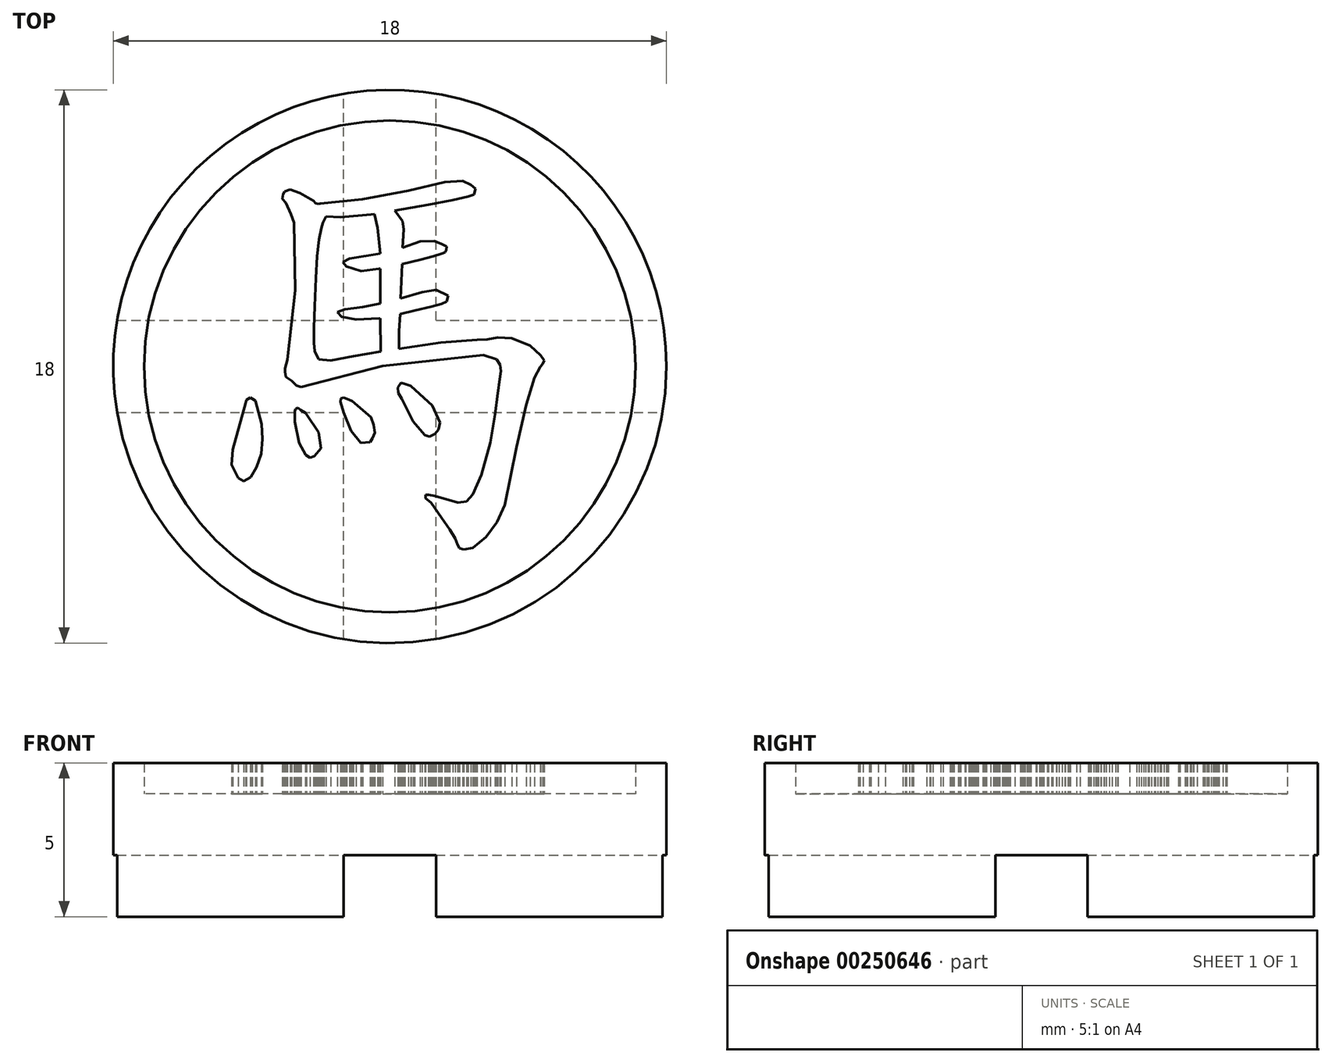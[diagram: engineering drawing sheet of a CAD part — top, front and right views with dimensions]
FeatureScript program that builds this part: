
annotation { "Feature Type Name" : "Feature", "Feature Type Description" : "" }
export const myFeature = defineFeature(function(context is Context, id is Id, definition is map)
    precondition{}
    {
        {
            var Q0;
            Q0=qCreatedBy(makeId("Top.planeOp"),FACE);
            var sketch = newSketch(context, id + "F0", { "sketchPlane" : qUnion([Q0])});
            skCircle(sketch, "E0", {"center": v(-31.33, 19.76) * mm, "radius": 9 * mm});
            skSolve(sketch);
        }
        {
            var Q0;
            Q0=qSketchRegion(id+"F0",true);
            extrude(context, id + "F1", {"entities" : qUnion([Q0]), "depth" : 4 * mm});
        }
        {
            var Q0;
            Q0=makeQuery(id+"F1.opExtrude","CAP_FACE",FACE,{"disambiguationData":[OSD([sQuery(id+"F0.wireOp",EDGE,"E0")])],"isStart":false});
            var sketch = newSketch(context, id + "F2", { "sketchPlane" : qUnion([Q0])});
            skCircle(sketch, "E1", {"center": v(-31.33, 19.76) * mm, "radius": 8 * mm});
            skCircle(sketch, "E2", {"center": v(-31.33, 19.76) * mm, "radius": 9 * mm});
            skSolve(sketch);
        }
        {
            var Q0;
            Q0=makeQuery(id+"F1.opExtrude","CAP_FACE",FACE,{"disambiguationData":[OSD([sQuery(id+"F0.wireOp",EDGE,"E0")])],"isStart":true});
            var sketch = newSketch(context, id + "F3", { "sketchPlane" : qUnion([Q0])});
            skLineSegment(sketch, "E3", {"start": v(-31.33, -19.76) * mm, "end": v(-22.33, -19.76) * mm, "construction": true});
            skLineSegment(sketch, "E4", {"start": v(-31.33, -19.76) * mm, "end": v(-31.33, -10.76) * mm, "construction": true});
            skLineSegment(sketch, "E5", {"start": v(-31.33, -19.76) * mm, "end": v(-40.33, -19.76) * mm, "construction": true});
            skLineSegment(sketch, "E6", {"start": v(-31.33, -19.76) * mm, "end": v(-31.33, -28.76) * mm, "construction": true});
            skLineSegment(sketch, "E7.bottom", {"start": v(-40.33, -28.76) * mm, "end": v(-22.33, -28.76) * mm});
            skLineSegment(sketch, "E7.top", {"start": v(-40.33, -10.76) * mm, "end": v(-22.33, -10.76) * mm});
            skLineSegment(sketch, "E7.left", {"start": v(-22.33, -10.76) * mm, "end": v(-22.33, -28.76) * mm});
            skLineSegment(sketch, "E7.right", {"start": v(-40.33, -10.76) * mm, "end": v(-40.33, -28.76) * mm});
            skPoint(sketch, "E8", {"position": v(-31.33, -28.76) * mm});
            skPoint(sketch, "E9", {"position": v(-40.33, -19.76) * mm});
            skPoint(sketch, "E10", {"position": v(-22.33, -19.76) * mm});
            skPoint(sketch, "E11", {"position": v(-31.33, -10.76) * mm});
            skLineSegment(sketch, "E12.bottom", {"start": v(-32.83, -10.76) * mm, "end": v(-29.83, -10.76) * mm});
            skLineSegment(sketch, "E12.top", {"start": v(-32.83, -28.76) * mm, "end": v(-29.83, -28.76) * mm});
            skLineSegment(sketch, "E12.left", {"start": v(-32.83, -10.76) * mm, "end": v(-32.83, -28.76) * mm});
            skLineSegment(sketch, "E12.right", {"start": v(-29.83, -10.76) * mm, "end": v(-29.83, -28.76) * mm});
            skLineSegment(sketch, "E13.bottom", {"start": v(-40.33, -18.26) * mm, "end": v(-22.33, -18.26) * mm});
            skLineSegment(sketch, "E13.top", {"start": v(-40.33, -21.26) * mm, "end": v(-22.33, -21.26) * mm});
            skLineSegment(sketch, "E13.left", {"start": v(-40.33, -18.26) * mm, "end": v(-40.33, -21.26) * mm});
            skLineSegment(sketch, "E13.right", {"start": v(-22.33, -18.26) * mm, "end": v(-22.33, -21.26) * mm});
            skSolve(sketch);
        }
        {
            var Q0;
            {var subQ1=sQuery(id+"F3.wireOp",EDGE,"E12.bottom");var subQ3=makeQuery(id+"F1.opExtrude","CAP_EDGE",EDGE,{"disambiguationData":[OSD([sQuery(id+"F0.wireOp",EDGE,"E0")])],"isStart":true});var subQ4=makeQuery(id+"F3.imprint","INTERSECT",VERTEX,{"derivedFrom":[subQ3,subQ1]});Q0=makeQuery(id+"F3.imprint","IMPRINT",FACE,{"disambiguationData":[TD([[makeQuery(id+"F3.imprint","IMPRINT",EDGE,{"disambiguationData":[TD([[subQ4,1.0]])],"derivedFrom":subQ3}),1.0]])]});}
            var Q1;
            {var subQ1=sQuery(id+"F3.wireOp",EDGE,"E12.bottom");var subQ3=makeQuery(id+"F1.opExtrude","CAP_EDGE",EDGE,{"disambiguationData":[OSD([sQuery(id+"F0.wireOp",EDGE,"E0")])],"isStart":true});var subQ4=makeQuery(id+"F3.imprint","INTERSECT",VERTEX,{"derivedFrom":[subQ3,subQ1]});Q1=makeQuery(id+"F3.imprint","IMPRINT",FACE,{"disambiguationData":[TD([[makeQuery(id+"F3.imprint","IMPRINT",EDGE,{"disambiguationData":[TD([[subQ4,-1.0]])],"derivedFrom":subQ3}),1.0]])]});}
            var Q2;
            {var subQ1=sQuery(id+"F3.wireOp",EDGE,"E12.top");var subQ3=makeQuery(id+"F1.opExtrude","CAP_EDGE",EDGE,{"disambiguationData":[OSD([sQuery(id+"F0.wireOp",EDGE,"E0")])],"isStart":true});var subQ4=makeQuery(id+"F3.imprint","INTERSECT",VERTEX,{"derivedFrom":[subQ3,subQ1]});Q2=makeQuery(id+"F3.imprint","IMPRINT",FACE,{"disambiguationData":[TD([[makeQuery(id+"F3.imprint","IMPRINT",EDGE,{"disambiguationData":[TD([[subQ4,-1.0]])],"derivedFrom":subQ3}),1.0]])]});}
            var Q3;
            {var subQ1=sQuery(id+"F3.wireOp",EDGE,"E12.top");var subQ3=makeQuery(id+"F1.opExtrude","CAP_EDGE",EDGE,{"disambiguationData":[OSD([sQuery(id+"F0.wireOp",EDGE,"E0")])],"isStart":true});var subQ4=makeQuery(id+"F3.imprint","INTERSECT",VERTEX,{"derivedFrom":[subQ3,subQ1]});Q3=makeQuery(id+"F3.imprint","IMPRINT",FACE,{"disambiguationData":[TD([[makeQuery(id+"F3.imprint","IMPRINT",EDGE,{"disambiguationData":[TD([[subQ4,1.0]])],"derivedFrom":subQ3}),1.0]])]});}
            var Q4;
            {var subQ0=sQuery(id+"F3.wireOp",EDGE,"E13.left");var subQ3=makeQuery(id+"F1.opExtrude","CAP_EDGE",EDGE,{"disambiguationData":[OSD([sQuery(id+"F0.wireOp",EDGE,"E0")])],"isStart":true});var subQ5=makeQuery(id+"F3.imprint","INTERSECT",VERTEX,{"derivedFrom":[subQ3,subQ0]});Q4=makeQuery(id+"F3.imprint","IMPRINT",FACE,{"disambiguationData":[TD([[makeQuery(id+"F3.imprint","IMPRINT",EDGE,{"disambiguationData":[TD([[subQ5,-1.0]])],"derivedFrom":subQ3}),1.0]])]});}
            var Q5;
            {var subQ0=sQuery(id+"F3.wireOp",EDGE,"E13.right");var subQ3=makeQuery(id+"F1.opExtrude","CAP_EDGE",EDGE,{"disambiguationData":[OSD([sQuery(id+"F0.wireOp",EDGE,"E0")])],"isStart":true});var subQ5=makeQuery(id+"F3.imprint","INTERSECT",VERTEX,{"derivedFrom":[subQ3,subQ0]});Q5=makeQuery(id+"F3.imprint","IMPRINT",FACE,{"disambiguationData":[TD([[makeQuery(id+"F3.imprint","IMPRINT",EDGE,{"disambiguationData":[TD([[subQ5,1.0]])],"derivedFrom":subQ3}),1.0]])]});}
            var Q6;
            {var subQ0=sQuery(id+"F3.wireOp",EDGE,"E13.left");var subQ3=makeQuery(id+"F1.opExtrude","CAP_EDGE",EDGE,{"disambiguationData":[OSD([sQuery(id+"F0.wireOp",EDGE,"E0")])],"isStart":true});var subQ5=makeQuery(id+"F3.imprint","INTERSECT",VERTEX,{"derivedFrom":[subQ3,subQ0]});Q6=makeQuery(id+"F3.imprint","IMPRINT",FACE,{"disambiguationData":[TD([[makeQuery(id+"F3.imprint","IMPRINT",EDGE,{"disambiguationData":[TD([[subQ5,1.0]])],"derivedFrom":subQ3}),1.0]])]});}
            var Q7;
            {var subQ0=sQuery(id+"F3.wireOp",EDGE,"E13.right");var subQ3=makeQuery(id+"F1.opExtrude","CAP_EDGE",EDGE,{"disambiguationData":[OSD([sQuery(id+"F0.wireOp",EDGE,"E0")])],"isStart":true});var subQ5=makeQuery(id+"F3.imprint","INTERSECT",VERTEX,{"derivedFrom":[subQ3,subQ0]});Q7=makeQuery(id+"F3.imprint","IMPRINT",FACE,{"disambiguationData":[TD([[makeQuery(id+"F3.imprint","IMPRINT",EDGE,{"disambiguationData":[TD([[subQ5,-1.0]])],"derivedFrom":subQ3}),1.0]])]});}
            var Q8;
            {var subQ3=makeQuery(id+"F1.opExtrude","CAP_EDGE",EDGE,{"disambiguationData":[OSD([sQuery(id+"F0.wireOp",EDGE,"E0")])],"isStart":true});var subQ5=sQuery(id+"F3.wireOp",EDGE,"E12.left");var subQ8=makeQuery(id+"F3.imprint","INTERSECT",VERTEX,{"disambiguationData":[OD(1.0)],"derivedFrom":[subQ3,subQ5]});Q8=makeQuery(id+"F3.imprint","IMPRINT",FACE,{"disambiguationData":[TD([[makeQuery(id+"F3.imprint","IMPRINT",EDGE,{"disambiguationData":[TD([[subQ8,-1.0]])],"derivedFrom":subQ3}),1.0]])]});}
            var Q9;
            {var subQ3=makeQuery(id+"F1.opExtrude","CAP_EDGE",EDGE,{"disambiguationData":[OSD([sQuery(id+"F0.wireOp",EDGE,"E0")])],"isStart":true});var subQ5=sQuery(id+"F3.wireOp",EDGE,"E12.right");var subQ8=makeQuery(id+"F3.imprint","INTERSECT",VERTEX,{"disambiguationData":[OD(1.0)],"derivedFrom":[subQ3,subQ5]});Q9=makeQuery(id+"F3.imprint","IMPRINT",FACE,{"disambiguationData":[TD([[makeQuery(id+"F3.imprint","IMPRINT",EDGE,{"disambiguationData":[TD([[subQ8,1.0]])],"derivedFrom":subQ3}),1.0]])]});}
            var Q10;
            {var subQ3=makeQuery(id+"F1.opExtrude","CAP_EDGE",EDGE,{"disambiguationData":[OSD([sQuery(id+"F0.wireOp",EDGE,"E0")])],"isStart":true});var subQ5=sQuery(id+"F3.wireOp",EDGE,"E12.left");var subQ8=makeQuery(id+"F3.imprint","INTERSECT",VERTEX,{"disambiguationData":[OD(0.0)],"derivedFrom":[subQ3,subQ5]});Q10=makeQuery(id+"F3.imprint","IMPRINT",FACE,{"disambiguationData":[TD([[makeQuery(id+"F3.imprint","IMPRINT",EDGE,{"disambiguationData":[TD([[subQ8,1.0]])],"derivedFrom":subQ3}),1.0]])]});}
            var Q11;
            {var subQ3=makeQuery(id+"F1.opExtrude","CAP_EDGE",EDGE,{"disambiguationData":[OSD([sQuery(id+"F0.wireOp",EDGE,"E0")])],"isStart":true});var subQ5=sQuery(id+"F3.wireOp",EDGE,"E12.right");var subQ8=makeQuery(id+"F3.imprint","INTERSECT",VERTEX,{"disambiguationData":[OD(0.0)],"derivedFrom":[subQ3,subQ5]});Q11=makeQuery(id+"F3.imprint","IMPRINT",FACE,{"disambiguationData":[TD([[makeQuery(id+"F3.imprint","IMPRINT",EDGE,{"disambiguationData":[TD([[subQ8,-1.0]])],"derivedFrom":subQ3}),1.0]])]});}
            var Q12;
            {var subQ2=sQuery(id+"F3.wireOp",EDGE,"E12.left");var subQ4=sQuery(id+"F3.wireOp",EDGE,"E13.bottom");var subQ8=makeQuery(id+"F3.imprint","INTERSECT",VERTEX,{"derivedFrom":[subQ2,subQ4]});Q12=makeQuery(id+"F3.imprint","IMPRINT",FACE,{"disambiguationData":[TD([[makeQuery(id+"F3.imprint","IMPRINT",EDGE,{"disambiguationData":[TD([[subQ8,1.0]])],"derivedFrom":subQ2}),1.0]])]});}
            var Q13;
            {var subQ1=sQuery(id+"F3.wireOp",EDGE,"E12.left");var subQ5=sQuery(id+"F3.wireOp",EDGE,"E13.bottom");var subQ6=makeQuery(id+"F3.imprint","INTERSECT",VERTEX,{"derivedFrom":[subQ1,subQ5]});Q13=makeQuery(id+"F3.imprint","IMPRINT",FACE,{"disambiguationData":[TD([[makeQuery(id+"F3.imprint","IMPRINT",EDGE,{"disambiguationData":[TD([[subQ6,-1.0]])],"derivedFrom":subQ1}),-1.0]])]});}
            var Q14;
            {var subQ0=sQuery(id+"F3.wireOp",EDGE,"E13.top");var subQ1=sQuery(id+"F3.wireOp",EDGE,"E12.left");var subQ2=makeQuery(id+"F3.imprint","INTERSECT",VERTEX,{"derivedFrom":[subQ1,subQ0]});Q14=makeQuery(id+"F3.imprint","IMPRINT",FACE,{"disambiguationData":[TD([[makeQuery(id+"F3.imprint","IMPRINT",EDGE,{"disambiguationData":[TD([[subQ2,-1.0]])],"derivedFrom":subQ1}),1.0]])]});}
            var Q15;
            {var subQ2=sQuery(id+"F3.wireOp",EDGE,"E13.bottom");var subQ5=sQuery(id+"F3.wireOp",EDGE,"E12.right");var subQ8=makeQuery(id+"F3.imprint","INTERSECT",VERTEX,{"derivedFrom":[subQ5,subQ2]});Q15=makeQuery(id+"F3.imprint","IMPRINT",FACE,{"disambiguationData":[TD([[makeQuery(id+"F3.imprint","IMPRINT",EDGE,{"disambiguationData":[TD([[subQ8,-1.0]])],"derivedFrom":subQ5}),1.0]])]});}
            var Q16;
            {var subQ0=sQuery(id+"F3.wireOp",EDGE,"E13.bottom");var subQ1=sQuery(id+"F3.wireOp",EDGE,"E12.left");var subQ2=makeQuery(id+"F3.imprint","INTERSECT",VERTEX,{"derivedFrom":[subQ1,subQ0]});Q16=makeQuery(id+"F3.imprint","IMPRINT",FACE,{"disambiguationData":[TD([[makeQuery(id+"F3.imprint","IMPRINT",EDGE,{"disambiguationData":[TD([[subQ2,-1.0]])],"derivedFrom":subQ1}),1.0]])]});}
            extrude(context, id + "F4", {"entities" : qUnion([Q0, Q1, Q2, Q3, Q4, Q5, Q6, Q7, Q8, Q9, Q10, Q11, Q12, Q13, Q14, Q15, Q16]), "operationType" : NewBodyOperationType.REMOVE, "oppositeDirection" : true, "depth" : 2 * mm});
        }
        {
            var Q0;
            Q0=qSketchRegion(id+"F2",true);
            var Q1;
            Q1=makeQuery(id+"F2.imprint","IMPRINT",FACE,{"disambiguationData":[TD([[makeQuery(id+"F2.imprint","IMPRINT",EDGE,{"derivedFrom":sQuery(id+"F2.wireOp",EDGE,"hKqnuJLd-dfdz-vJIs-yDKo-c4hLNRw30SuP")}),-1.0]])]});
            extrude(context, id + "F5", {"entities" : qUnion([Q0, Q1]), "operationType" : NewBodyOperationType.ADD, "depth" : 1 * mm});
        }
        {
            var Q0;
            Q0=makeQuery(id+"F1.opExtrude","CAP_FACE",FACE,{"disambiguationData":[OSD([sQuery(id+"F0.wireOp",EDGE,"E0")])],"isStart":false});
            var sketch = newSketch(context, id + "F6", { "sketchPlane" : qUnion([Q0])});
            skLineSegment(sketch, "E14", {"start": v(-30.99, 21.98) * mm, "end": v(-30.93, 23.1) * mm});
            skLineSegment(sketch, "E15", {"start": v(-30.93, 23.1) * mm, "end": v(-30.34, 23.23) * mm});
            skLineSegment(sketch, "E16", {"start": v(-30.34, 23.23) * mm, "end": v(-29.9, 23.35) * mm});
            skLineSegment(sketch, "E17", {"start": v(-29.9, 23.35) * mm, "end": v(-29.64, 23.43) * mm});
            skLineSegment(sketch, "E18", {"start": v(-29.64, 23.43) * mm, "end": v(-29.54, 23.47) * mm});
            skLineSegment(sketch, "E19", {"start": v(-29.54, 23.47) * mm, "end": v(-29.5, 23.55) * mm});
            skLineSegment(sketch, "E20", {"start": v(-29.5, 23.55) * mm, "end": v(-29.48, 23.66) * mm});
            skLineSegment(sketch, "E21", {"start": v(-29.48, 23.66) * mm, "end": v(-29.65, 23.75) * mm});
            skLineSegment(sketch, "E22", {"start": v(-29.65, 23.75) * mm, "end": v(-29.89, 23.84) * mm});
            skLineSegment(sketch, "E23", {"start": v(-29.89, 23.84) * mm, "end": v(-30.35, 23.82) * mm});
            skLineSegment(sketch, "E24", {"start": v(-30.35, 23.82) * mm, "end": v(-30.92, 23.63) * mm});
            skLineSegment(sketch, "E25", {"start": v(-30.92, 23.63) * mm, "end": v(-30.88, 24.23) * mm});
            skLineSegment(sketch, "E26", {"start": v(-30.88, 24.23) * mm, "end": v(-30.92, 24.49) * mm});
            skLineSegment(sketch, "E27", {"start": v(-30.92, 24.49) * mm, "end": v(-31.16, 24.81) * mm});
            skLineSegment(sketch, "E28", {"start": v(-31.16, 24.81) * mm, "end": v(-31.17, 24.83) * mm});
            skLineSegment(sketch, "E29", {"start": v(-31.17, 24.83) * mm, "end": v(-30.07, 25.02) * mm});
            skLineSegment(sketch, "E30", {"start": v(-30.07, 25.02) * mm, "end": v(-29.28, 25.18) * mm});
            skLineSegment(sketch, "E31", {"start": v(-29.28, 25.18) * mm, "end": v(-28.78, 25.3) * mm});
            skLineSegment(sketch, "E32", {"start": v(-28.78, 25.3) * mm, "end": v(-28.6, 25.35) * mm});
            skLineSegment(sketch, "E33", {"start": v(-28.6, 25.35) * mm, "end": v(-28.54, 25.55) * mm});
            skLineSegment(sketch, "E34", {"start": v(-28.54, 25.55) * mm, "end": v(-28.69, 25.66) * mm});
            skLineSegment(sketch, "E35", {"start": v(-28.69, 25.66) * mm, "end": v(-28.96, 25.8) * mm});
            skLineSegment(sketch, "E36", {"start": v(-28.96, 25.8) * mm, "end": v(-29.55, 25.76) * mm});
            skLineSegment(sketch, "E37", {"start": v(-29.55, 25.76) * mm, "end": v(-30.72, 25.48) * mm});
            skLineSegment(sketch, "E38", {"start": v(-30.72, 25.48) * mm, "end": v(-32.23, 25.2) * mm});
            skLineSegment(sketch, "E39", {"start": v(-32.23, 25.2) * mm, "end": v(-33.6, 25.06) * mm});
            skLineSegment(sketch, "E40", {"start": v(-33.6, 25.06) * mm, "end": v(-33.66, 25.04) * mm});
            skLineSegment(sketch, "E41", {"start": v(-33.66, 25.04) * mm, "end": v(-33.75, 25.08) * mm});
            skLineSegment(sketch, "E42", {"start": v(-33.75, 25.08) * mm, "end": v(-33.81, 25.15) * mm});
            skLineSegment(sketch, "E43", {"start": v(-33.81, 25.15) * mm, "end": v(-34.25, 25.4) * mm});
            skLineSegment(sketch, "E44", {"start": v(-34.25, 25.4) * mm, "end": v(-34.57, 25.52) * mm});
            skLineSegment(sketch, "E45", {"start": v(-34.57, 25.52) * mm, "end": v(-34.75, 25.45) * mm});
            skLineSegment(sketch, "E46", {"start": v(-34.75, 25.45) * mm, "end": v(-34.8, 25.36) * mm});
            skLineSegment(sketch, "E47", {"start": v(-34.8, 25.36) * mm, "end": v(-34.82, 25.2) * mm});
            skLineSegment(sketch, "E48", {"start": v(-34.82, 25.2) * mm, "end": v(-34.71, 25.08) * mm});
            skLineSegment(sketch, "E49", {"start": v(-34.71, 25.08) * mm, "end": v(-34.54, 24.72) * mm});
            skLineSegment(sketch, "E50", {"start": v(-34.54, 24.72) * mm, "end": v(-34.45, 24.44) * mm});
            skLineSegment(sketch, "E51", {"start": v(-34.45, 24.44) * mm, "end": v(-34.41, 22.24) * mm});
            skLineSegment(sketch, "E52", {"start": v(-34.41, 22.24) * mm, "end": v(-34.66, 19.98) * mm});
            skLineSegment(sketch, "E53", {"start": v(-34.66, 19.98) * mm, "end": v(-34.74, 19.7) * mm});
            skLineSegment(sketch, "E54", {"start": v(-34.74, 19.7) * mm, "end": v(-34.74, 19.58) * mm});
            skLineSegment(sketch, "E55", {"start": v(-34.74, 19.58) * mm, "end": v(-34.7, 19.42) * mm});
            skLineSegment(sketch, "E56", {"start": v(-34.7, 19.42) * mm, "end": v(-34.53, 19.29) * mm});
            skLineSegment(sketch, "E57", {"start": v(-34.53, 19.29) * mm, "end": v(-34.37, 19.14) * mm});
            skLineSegment(sketch, "E58", {"start": v(-34.37, 19.14) * mm, "end": v(-34.22, 19.1) * mm});
            skLineSegment(sketch, "E59", {"start": v(-34.22, 19.1) * mm, "end": v(-31.57, 19.77) * mm});
            skLineSegment(sketch, "E60", {"start": v(-31.57, 19.77) * mm, "end": v(-28.29, 20.13) * mm});
            skLineSegment(sketch, "E61", {"start": v(-28.29, 20.13) * mm, "end": v(-27.86, 20) * mm});
            skLineSegment(sketch, "E62", {"start": v(-27.86, 20) * mm, "end": v(-27.74, 19.81) * mm});
            skLineSegment(sketch, "E63", {"start": v(-27.74, 19.81) * mm, "end": v(-27.71, 19.6) * mm});
            skLineSegment(sketch, "E64", {"start": v(-27.71, 19.6) * mm, "end": v(-27.76, 19.34) * mm});
            skLineSegment(sketch, "E65", {"start": v(-27.76, 19.34) * mm, "end": v(-27.82, 18.88) * mm});
            skLineSegment(sketch, "E66", {"start": v(-27.82, 18.88) * mm, "end": v(-27.91, 18.2) * mm});
            skLineSegment(sketch, "E67", {"start": v(-27.91, 18.2) * mm, "end": v(-28.06, 17.29) * mm});
            skLineSegment(sketch, "E68", {"start": v(-28.06, 17.29) * mm, "end": v(-28.35, 16.24) * mm});
            skLineSegment(sketch, "E69", {"start": v(-28.35, 16.24) * mm, "end": v(-28.63, 15.6) * mm});
            skLineSegment(sketch, "E70", {"start": v(-28.63, 15.6) * mm, "end": v(-28.84, 15.37) * mm});
            skLineSegment(sketch, "E71", {"start": v(-28.84, 15.37) * mm, "end": v(-29.11, 15.33) * mm});
            skLineSegment(sketch, "E72", {"start": v(-29.11, 15.33) * mm, "end": v(-29.86, 15.55) * mm});
            skLineSegment(sketch, "E73", {"start": v(-29.86, 15.55) * mm, "end": v(-30.06, 15.59) * mm});
            skLineSegment(sketch, "E74", {"start": v(-30.06, 15.59) * mm, "end": v(-30.16, 15.58) * mm});
            skLineSegment(sketch, "E75", {"start": v(-30.16, 15.58) * mm, "end": v(-30.17, 15.46) * mm});
            skLineSegment(sketch, "E76", {"start": v(-30.17, 15.46) * mm, "end": v(-30, 15.33) * mm});
            skLineSegment(sketch, "E77", {"start": v(-30, 15.33) * mm, "end": v(-29.65, 14.84) * mm});
            skLineSegment(sketch, "E78", {"start": v(-29.65, 14.84) * mm, "end": v(-29.38, 14.45) * mm});
            skLineSegment(sketch, "E79", {"start": v(-29.38, 14.45) * mm, "end": v(-29.2, 14.16) * mm});
            skLineSegment(sketch, "E80", {"start": v(-29.2, 14.16) * mm, "end": v(-29.13, 13.96) * mm});
            skLineSegment(sketch, "E81", {"start": v(-29.13, 13.96) * mm, "end": v(-29.06, 13.85) * mm});
            skLineSegment(sketch, "E82", {"start": v(-29.06, 13.85) * mm, "end": v(-28.93, 13.8) * mm});
            skLineSegment(sketch, "E83", {"start": v(-28.93, 13.8) * mm, "end": v(-28.64, 13.86) * mm});
            skLineSegment(sketch, "E84", {"start": v(-28.64, 13.86) * mm, "end": v(-28.2, 14.21) * mm});
            skLineSegment(sketch, "E85", {"start": v(-28.2, 14.21) * mm, "end": v(-27.85, 14.69) * mm});
            skLineSegment(sketch, "E86", {"start": v(-27.85, 14.69) * mm, "end": v(-27.6, 15.25) * mm});
            skLineSegment(sketch, "E87", {"start": v(-27.6, 15.25) * mm, "end": v(-27.22, 17.14) * mm});
            skLineSegment(sketch, "E88", {"start": v(-27.22, 17.14) * mm, "end": v(-26.89, 18.52) * mm});
            skLineSegment(sketch, "E89", {"start": v(-26.89, 18.52) * mm, "end": v(-26.63, 19.4) * mm});
            skLineSegment(sketch, "E90", {"start": v(-26.63, 19.4) * mm, "end": v(-26.43, 19.75) * mm});
            skLineSegment(sketch, "E91", {"start": v(-26.43, 19.75) * mm, "end": v(-26.36, 19.83) * mm});
            skLineSegment(sketch, "E92", {"start": v(-26.36, 19.83) * mm, "end": v(-26.31, 19.95) * mm});
            skLineSegment(sketch, "E93", {"start": v(-26.31, 19.95) * mm, "end": v(-26.43, 20.12) * mm});
            skLineSegment(sketch, "E94", {"start": v(-26.43, 20.12) * mm, "end": v(-26.77, 20.43) * mm});
            skLineSegment(sketch, "E95", {"start": v(-26.77, 20.43) * mm, "end": v(-27.36, 20.68) * mm});
            skLineSegment(sketch, "E96", {"start": v(-27.36, 20.68) * mm, "end": v(-27.82, 20.7) * mm});
            skLineSegment(sketch, "E97", {"start": v(-27.82, 20.7) * mm, "end": v(-28.16, 20.64) * mm});
            skLineSegment(sketch, "E98", {"start": v(-28.16, 20.64) * mm, "end": v(-28.49, 20.62) * mm});
            skLineSegment(sketch, "E99", {"start": v(-28.49, 20.62) * mm, "end": v(-29.67, 20.53) * mm});
            skLineSegment(sketch, "E100", {"start": v(-29.67, 20.53) * mm, "end": v(-31.03, 20.33) * mm});
            skLineSegment(sketch, "E101", {"start": v(-31.03, 20.33) * mm, "end": v(-31.04, 20.9) * mm});
            skLineSegment(sketch, "E102", {"start": v(-31.04, 20.9) * mm, "end": v(-31, 21.46) * mm});
            skLineSegment(sketch, "E103", {"start": v(-31, 21.46) * mm, "end": v(-30.53, 21.58) * mm});
            skLineSegment(sketch, "E104", {"start": v(-30.53, 21.58) * mm, "end": v(-29.98, 21.7) * mm});
            skLineSegment(sketch, "E105", {"start": v(-29.98, 21.7) * mm, "end": v(-29.65, 21.8) * mm});
            skLineSegment(sketch, "E106", {"start": v(-29.65, 21.8) * mm, "end": v(-29.48, 21.87) * mm});
            skLineSegment(sketch, "E107", {"start": v(-29.48, 21.87) * mm, "end": v(-29.43, 22.06) * mm});
            skLineSegment(sketch, "E108", {"start": v(-29.43, 22.06) * mm, "end": v(-29.83, 22.25) * mm});
            skLineSegment(sketch, "E109", {"start": v(-29.83, 22.25) * mm, "end": v(-30.29, 22.18) * mm});
            skLineSegment(sketch, "E110", {"start": v(-30.29, 22.18) * mm, "end": v(-30.99, 21.98) * mm});
            skLineSegment(sketch, "E111", {"start": v(-31.64, 21.8) * mm, "end": v(-32.2, 21.69) * mm});
            skLineSegment(sketch, "E112", {"start": v(-32.2, 21.69) * mm, "end": v(-32.8, 21.62) * mm});
            skLineSegment(sketch, "E113", {"start": v(-32.8, 21.62) * mm, "end": v(-33.03, 21.53) * mm});
            skLineSegment(sketch, "E114", {"start": v(-33.03, 21.53) * mm, "end": v(-32.9, 21.38) * mm});
            skLineSegment(sketch, "E115", {"start": v(-32.9, 21.38) * mm, "end": v(-32.43, 21.28) * mm});
            skLineSegment(sketch, "E116", {"start": v(-32.43, 21.28) * mm, "end": v(-31.68, 21.33) * mm});
            skLineSegment(sketch, "E117", {"start": v(-31.68, 21.33) * mm, "end": v(-31.69, 21.3) * mm});
            skLineSegment(sketch, "E118", {"start": v(-31.69, 21.3) * mm, "end": v(-31.64, 21.33) * mm});
            skLineSegment(sketch, "E119", {"start": v(-31.64, 21.33) * mm, "end": v(-31.62, 20.25) * mm});
            skLineSegment(sketch, "E120", {"start": v(-31.62, 20.25) * mm, "end": v(-32.52, 20.1) * mm});
            skLineSegment(sketch, "E121", {"start": v(-32.52, 20.1) * mm, "end": v(-33.25, 19.95) * mm});
            skLineSegment(sketch, "E122", {"start": v(-33.25, 19.95) * mm, "end": v(-33.65, 20) * mm});
            skLineSegment(sketch, "E123", {"start": v(-33.65, 20) * mm, "end": v(-33.77, 20.26) * mm});
            skLineSegment(sketch, "E124", {"start": v(-33.77, 20.26) * mm, "end": v(-33.8, 20.52) * mm});
            skLineSegment(sketch, "E125", {"start": v(-33.8, 20.52) * mm, "end": v(-33.8, 21.01) * mm});
            skLineSegment(sketch, "E126", {"start": v(-33.8, 21.01) * mm, "end": v(-33.78, 21.72) * mm});
            skLineSegment(sketch, "E127", {"start": v(-33.78, 21.72) * mm, "end": v(-33.74, 22.63) * mm});
            skLineSegment(sketch, "E128", {"start": v(-33.74, 22.63) * mm, "end": v(-33.7, 23.34) * mm});
            skLineSegment(sketch, "E129", {"start": v(-33.7, 23.34) * mm, "end": v(-33.63, 23.89) * mm});
            skLineSegment(sketch, "E130", {"start": v(-33.63, 23.89) * mm, "end": v(-33.57, 24.26) * mm});
            skLineSegment(sketch, "E131", {"start": v(-33.57, 24.26) * mm, "end": v(-33.5, 24.44) * mm});
            skLineSegment(sketch, "E132", {"start": v(-33.5, 24.44) * mm, "end": v(-33.47, 24.51) * mm});
            skLineSegment(sketch, "E133", {"start": v(-33.47, 24.51) * mm, "end": v(-33.4, 24.64) * mm});
            skLineSegment(sketch, "E134", {"start": v(-33.4, 24.64) * mm, "end": v(-32.94, 24.6) * mm});
            skLineSegment(sketch, "E135", {"start": v(-32.94, 24.6) * mm, "end": v(-31.94, 24.7) * mm});
            skLineSegment(sketch, "E136", {"start": v(-31.94, 24.7) * mm, "end": v(-31.84, 24.72) * mm});
            skLineSegment(sketch, "E137", {"start": v(-31.84, 24.72) * mm, "end": v(-31.73, 24.27) * mm});
            skLineSegment(sketch, "E138", {"start": v(-31.73, 24.27) * mm, "end": v(-31.64, 23.43) * mm});
            skLineSegment(sketch, "E139", {"start": v(-31.64, 23.43) * mm, "end": v(-32.64, 23.27) * mm});
            skLineSegment(sketch, "E140", {"start": v(-32.64, 23.27) * mm, "end": v(-32.87, 23.15) * mm});
            skLineSegment(sketch, "E141", {"start": v(-32.87, 23.15) * mm, "end": v(-32.75, 23.02) * mm});
            skLineSegment(sketch, "E142", {"start": v(-32.75, 23.02) * mm, "end": v(-32.26, 22.86) * mm});
            skLineSegment(sketch, "E143", {"start": v(-32.26, 22.86) * mm, "end": v(-31.7, 22.93) * mm});
            skLineSegment(sketch, "E144", {"start": v(-31.7, 22.93) * mm, "end": v(-31.64, 22.93) * mm});
            skLineSegment(sketch, "E145", {"start": v(-31.64, 22.93) * mm, "end": v(-31.64, 21.8) * mm});
            skLineSegment(sketch, "E146", {"start": v(-36.02, 18.57) * mm, "end": v(-36.45, 17.05) * mm});
            skLineSegment(sketch, "E147", {"start": v(-36.45, 17.05) * mm, "end": v(-36.49, 16.57) * mm});
            skLineSegment(sketch, "E148", {"start": v(-36.49, 16.57) * mm, "end": v(-36.26, 16.13) * mm});
            skLineSegment(sketch, "E149", {"start": v(-36.26, 16.13) * mm, "end": v(-36.08, 16.03) * mm});
            skLineSegment(sketch, "E150", {"start": v(-36.08, 16.03) * mm, "end": v(-35.86, 16.16) * mm});
            skLineSegment(sketch, "E151", {"start": v(-35.86, 16.16) * mm, "end": v(-35.67, 16.49) * mm});
            skLineSegment(sketch, "E152", {"start": v(-35.67, 16.49) * mm, "end": v(-35.52, 16.92) * mm});
            skLineSegment(sketch, "E153", {"start": v(-35.52, 16.92) * mm, "end": v(-35.48, 17.4) * mm});
            skLineSegment(sketch, "E154", {"start": v(-35.48, 17.4) * mm, "end": v(-35.5, 17.88) * mm});
            skLineSegment(sketch, "E155", {"start": v(-35.5, 17.88) * mm, "end": v(-35.7, 18.65) * mm});
            skLineSegment(sketch, "E156", {"start": v(-35.7, 18.65) * mm, "end": v(-35.8, 18.7) * mm});
            skLineSegment(sketch, "E157", {"start": v(-35.8, 18.7) * mm, "end": v(-35.87, 18.74) * mm});
            skLineSegment(sketch, "E158", {"start": v(-35.87, 18.74) * mm, "end": v(-36, 18.67) * mm});
            skLineSegment(sketch, "E159", {"start": v(-36, 18.67) * mm, "end": v(-36.02, 18.57) * mm});
            skLineSegment(sketch, "E160", {"start": v(-34.42, 17.96) * mm, "end": v(-34.28, 17.28) * mm});
            skLineSegment(sketch, "E161", {"start": v(-34.28, 17.28) * mm, "end": v(-34.06, 16.88) * mm});
            skLineSegment(sketch, "E162", {"start": v(-34.06, 16.88) * mm, "end": v(-33.93, 16.8) * mm});
            skLineSegment(sketch, "E163", {"start": v(-33.93, 16.8) * mm, "end": v(-33.78, 16.84) * mm});
            skLineSegment(sketch, "E164", {"start": v(-33.78, 16.84) * mm, "end": v(-33.57, 17.09) * mm});
            skLineSegment(sketch, "E165", {"start": v(-33.57, 17.09) * mm, "end": v(-33.65, 17.61) * mm});
            skLineSegment(sketch, "E166", {"start": v(-33.65, 17.61) * mm, "end": v(-34.04, 18.2) * mm});
            skLineSegment(sketch, "E167", {"start": v(-34.04, 18.2) * mm, "end": v(-34.08, 18.25) * mm});
            skLineSegment(sketch, "E168", {"start": v(-34.08, 18.25) * mm, "end": v(-34.23, 18.33) * mm});
            skLineSegment(sketch, "E169", {"start": v(-34.23, 18.33) * mm, "end": v(-34.32, 18.4) * mm});
            skLineSegment(sketch, "E170", {"start": v(-34.32, 18.4) * mm, "end": v(-34.4, 18.38) * mm});
            skLineSegment(sketch, "E171", {"start": v(-34.4, 18.38) * mm, "end": v(-34.42, 18.3) * mm});
            skLineSegment(sketch, "E172", {"start": v(-34.42, 18.3) * mm, "end": v(-34.42, 17.96) * mm});
            skLineSegment(sketch, "E173", {"start": v(-32.84, 18.26) * mm, "end": v(-32.6, 17.67) * mm});
            skLineSegment(sketch, "E174", {"start": v(-32.6, 17.67) * mm, "end": v(-32.28, 17.28) * mm});
            skLineSegment(sketch, "E175", {"start": v(-32.28, 17.28) * mm, "end": v(-31.97, 17.3) * mm});
            skLineSegment(sketch, "E176", {"start": v(-31.97, 17.3) * mm, "end": v(-31.9, 17.43) * mm});
            skLineSegment(sketch, "E177", {"start": v(-31.9, 17.43) * mm, "end": v(-31.82, 17.6) * mm});
            skLineSegment(sketch, "E178", {"start": v(-31.82, 17.6) * mm, "end": v(-31.85, 17.86) * mm});
            skLineSegment(sketch, "E179", {"start": v(-31.85, 17.86) * mm, "end": v(-31.94, 18.12) * mm});
            skLineSegment(sketch, "E180", {"start": v(-31.94, 18.12) * mm, "end": v(-32.56, 18.64) * mm});
            skLineSegment(sketch, "E181", {"start": v(-32.56, 18.64) * mm, "end": v(-32.73, 18.7) * mm});
            skLineSegment(sketch, "E182", {"start": v(-32.73, 18.7) * mm, "end": v(-32.84, 18.74) * mm});
            skLineSegment(sketch, "E183", {"start": v(-32.84, 18.74) * mm, "end": v(-32.92, 18.72) * mm});
            skLineSegment(sketch, "E184", {"start": v(-32.92, 18.72) * mm, "end": v(-32.93, 18.6) * mm});
            skLineSegment(sketch, "E185", {"start": v(-32.93, 18.6) * mm, "end": v(-32.84, 18.26) * mm});
            skLineSegment(sketch, "E186", {"start": v(-30.95, 18.7) * mm, "end": v(-30.58, 17.97) * mm});
            skLineSegment(sketch, "E187", {"start": v(-30.58, 17.97) * mm, "end": v(-30.2, 17.53) * mm});
            skLineSegment(sketch, "E188", {"start": v(-30.2, 17.53) * mm, "end": v(-30.04, 17.48) * mm});
            skLineSegment(sketch, "E189", {"start": v(-30.04, 17.48) * mm, "end": v(-29.86, 17.57) * mm});
            skLineSegment(sketch, "E190", {"start": v(-29.86, 17.57) * mm, "end": v(-29.76, 17.7) * mm});
            skLineSegment(sketch, "E191", {"start": v(-29.76, 17.7) * mm, "end": v(-29.7, 17.93) * mm});
            skLineSegment(sketch, "E192", {"start": v(-29.7, 17.93) * mm, "end": v(-29.96, 18.5) * mm});
            skLineSegment(sketch, "E193", {"start": v(-29.96, 18.5) * mm, "end": v(-30.64, 19.11) * mm});
            skLineSegment(sketch, "E194", {"start": v(-30.64, 19.11) * mm, "end": v(-30.65, 19.13) * mm});
            skLineSegment(sketch, "E195", {"start": v(-30.65, 19.13) * mm, "end": v(-30.83, 19.2) * mm});
            skLineSegment(sketch, "E196", {"start": v(-30.83, 19.2) * mm, "end": v(-30.97, 19.23) * mm});
            skLineSegment(sketch, "E197", {"start": v(-30.97, 19.23) * mm, "end": v(-31.06, 19.08) * mm});
            skLineSegment(sketch, "E198", {"start": v(-31.06, 19.08) * mm, "end": v(-31.06, 18.9) * mm});
            skLineSegment(sketch, "E199", {"start": v(-31.06, 18.9) * mm, "end": v(-30.95, 18.7) * mm});
            skSolve(sketch);
        }
        {
            var Q0;
            Q0 = qSketchRegion(id + "F6", true);
            extrude(context, id + "F7", {"entities" : qUnion([Q0]), "operationType" : NewBodyOperationType.ADD, "depth" : 1 * mm});
        }
    });
